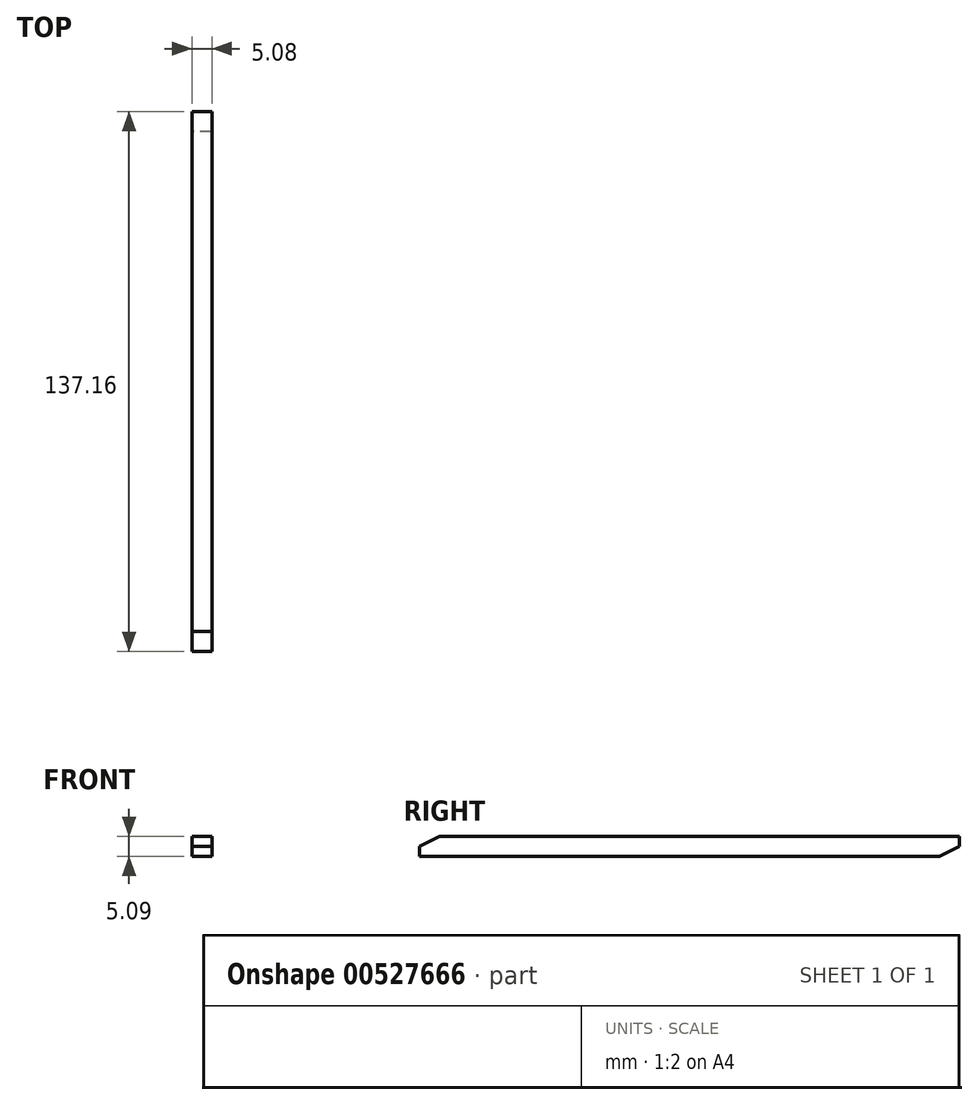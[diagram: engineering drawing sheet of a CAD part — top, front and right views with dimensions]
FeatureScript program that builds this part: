
annotation { "Feature Type Name" : "Feature", "Feature Type Description" : "" }
export const myFeature = defineFeature(function(context is Context, id is Id, definition is map)
    precondition{}
    {
        {
            var Q0;
            Q0=qCreatedBy(makeId("Right.planeOp"),FACE);
            var sketch = newSketch(context, id + "F0", { "sketchPlane" : qUnion([Q0])});
            skLineSegment(sketch, "E0.bottom", {"start": v(-75.7, 8.88) * mm, "end": v(51.3, 8.88) * mm});
            skLineSegment(sketch, "E0.top", {"start": v(-75.7, 3.8) * mm, "end": v(51.3, 3.8) * mm});
            skLineSegment(sketch, "E0.left", {"start": v(-75.7, 8.88) * mm, "end": v(-75.7, 3.8) * mm});
            skLineSegment(sketch, "E0.right", {"start": v(51.3, 8.88) * mm, "end": v(51.3, 3.8) * mm});
            skLineSegment(sketch, "E1.bottom", {"start": v(51.3, 8.88) * mm, "end": v(51.3, 8.88) * mm});
            skLineSegment(sketch, "E1.top", {"start": v(51.3, 6.33) * mm, "end": v(51.3, 6.33) * mm});
            skLineSegment(sketch, "E1.left", {"start": v(51.3, 8.88) * mm, "end": v(51.3, 6.33) * mm});
            skLineSegment(sketch, "E1.right", {"start": v(51.3, 8.88) * mm, "end": v(51.3, 6.33) * mm});
            skLineSegment(sketch, "E2.bottom", {"start": v(51.3, 6.33) * mm, "end": v(56.38, 6.33) * mm});
            skLineSegment(sketch, "E2.top", {"start": v(51.3, 8.88) * mm, "end": v(56.38, 8.88) * mm});
            skLineSegment(sketch, "E2.left", {"start": v(51.3, 6.33) * mm, "end": v(51.3, 8.88) * mm});
            skLineSegment(sketch, "E2.right", {"start": v(56.38, 6.33) * mm, "end": v(56.38, 8.88) * mm});
            skLineSegment(sketch, "E3", {"start": v(51.3, 3.8) * mm, "end": v(56.38, 6.33) * mm});
            skPoint(sketch, "E4.oppositeSnap0", {"position": v(-75.7, 6.33) * mm});
            skLineSegment(sketch, "E4.top", {"start": v(-75.7, 6.33) * mm, "end": v(-80.78, 6.33) * mm});
            skLineSegment(sketch, "E4.left", {"start": v(-75.7, 8.88) * mm, "end": v(-75.7, 6.33) * mm});
            skLineSegment(sketch, "E5.bottom", {"start": v(-80.78, 6.33) * mm, "end": v(-75.7, 6.33) * mm});
            skLineSegment(sketch, "E5.top", {"start": v(-80.78, 3.8) * mm, "end": v(-75.7, 3.8) * mm});
            skLineSegment(sketch, "E5.left", {"start": v(-80.78, 6.33) * mm, "end": v(-80.78, 3.8) * mm});
            skLineSegment(sketch, "E5.right", {"start": v(-75.7, 6.33) * mm, "end": v(-75.7, 3.8) * mm});
            skLineSegment(sketch, "E6", {"start": v(-80.78, 6.33) * mm, "end": v(-75.7, 8.88) * mm});
            skSolve(sketch);
        }
        {
            var Q0;
            Q0 = qSketchRegion(id + "F0", true);
            extrude(context, id + "F1", {"entities" : qUnion([Q0]), "depth" : 5.08 * mm, "offsetDistance" : 25.4 * mm});
        }
    });
